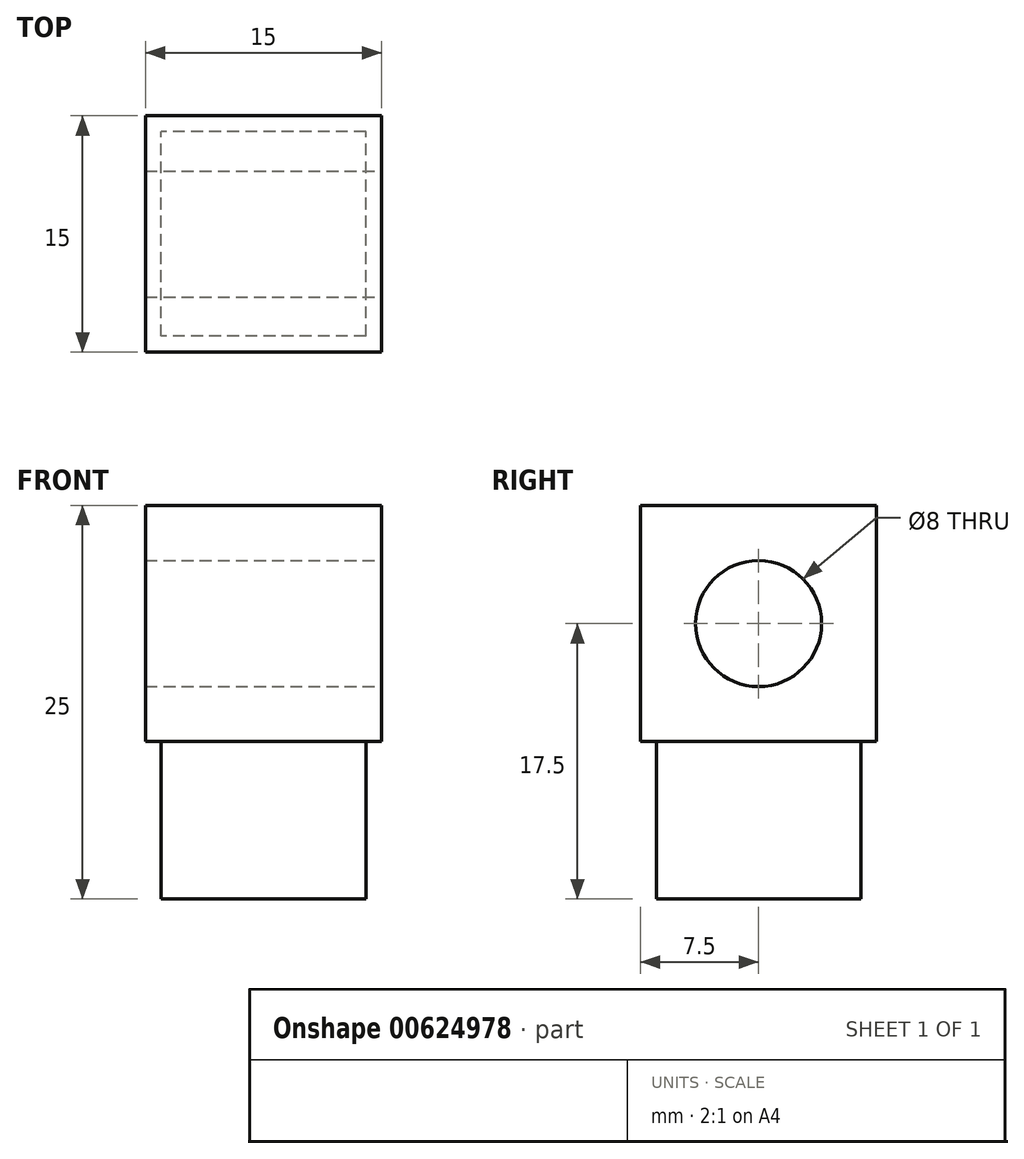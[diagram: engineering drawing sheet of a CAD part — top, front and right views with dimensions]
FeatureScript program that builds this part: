
annotation { "Feature Type Name" : "Feature", "Feature Type Description" : "" }
export const myFeature = defineFeature(function(context is Context, id is Id, definition is map)
    precondition{}
    {
        {
            var Q0;
            Q0=qCreatedBy(makeId("Top.planeOp"),FACE);
            var sketch = newSketch(context, id + "F0", { "sketchPlane" : qUnion([Q0])});
            skLineSegment(sketch, "E0.bottom", {"start": v(6.5, -6.5) * mm, "end": v(-6.5, -6.5) * mm});
            skLineSegment(sketch, "E0.top", {"start": v(6.5, 6.5) * mm, "end": v(-6.5, 6.5) * mm});
            skLineSegment(sketch, "E0.left", {"start": v(6.5, -6.5) * mm, "end": v(6.5, 6.5) * mm});
            skLineSegment(sketch, "E0.right", {"start": v(-6.5, -6.5) * mm, "end": v(-6.5, 6.5) * mm});
            skPoint(sketch, "E0.middle", {"position": v(0, 0) * mm});
            skSolve(sketch);
        }
        {
            var Q0;
            Q0=makeQuery(id+"F0.imprint","IMPRINT",FACE,{"disambiguationData":[TD([[makeQuery(id+"F0.imprint","IMPRINT",EDGE,{"derivedFrom":sQuery(id+"F0.wireOp",EDGE,"E0.bottom")}),-1.0]])]});
            extrude(context, id + "F1", {"entities" : qUnion([Q0]), "depth" : 10 * mm, "offsetDistance" : 25 * mm});
        }
        {
            var Q0;
            Q0=makeQuery(id+"F1.opExtrude","CAP_FACE",FACE,{"disambiguationData":[OSD([sQuery(id+"F0.wireOp",EDGE,"E0.bottom"),sQuery(id+"F0.wireOp",EDGE,"E0.top"),sQuery(id+"F0.wireOp",EDGE,"E0.left"),sQuery(id+"F0.wireOp",EDGE,"E0.right")])],"isStart":false});
            var sketch = newSketch(context, id + "F2", { "sketchPlane" : qUnion([Q0])});
            skLineSegment(sketch, "E1.bottom", {"start": v(7.5, -7.5) * mm, "end": v(-7.5, -7.5) * mm});
            skLineSegment(sketch, "E1.top", {"start": v(7.5, 7.5) * mm, "end": v(-7.5, 7.5) * mm});
            skLineSegment(sketch, "E1.left", {"start": v(7.5, -7.5) * mm, "end": v(7.5, 7.5) * mm});
            skLineSegment(sketch, "E1.right", {"start": v(-7.5, -7.5) * mm, "end": v(-7.5, 7.5) * mm});
            skPoint(sketch, "E1.middle", {"position": v(0, 0) * mm});
            skSolve(sketch);
        }
        {
            var Q0;
            Q0=makeQuery(id+"F2.imprint","IMPRINT",FACE,{"disambiguationData":[TD([[makeQuery(id+"F2.imprint","IMPRINT",EDGE,{"derivedFrom":makeQuery(id+"F1.opExtrude","CAP_EDGE",EDGE,{"disambiguationData":[OSD([sQuery(id+"F0.wireOp",EDGE,"E0.bottom")])],"isStart":false})}),-1.0]])]});
            var Q1;
            Q1=makeQuery(id+"F2.imprint","IMPRINT",FACE,{"disambiguationData":[TD([[makeQuery(id+"F2.imprint","IMPRINT",EDGE,{"derivedFrom":sQuery(id+"F2.wireOp",EDGE,"E1.bottom")}),-1.0]])]});
            extrude(context, id + "F3", {"entities" : qUnion([Q0, Q1]), "operationType" : NewBodyOperationType.ADD, "depth" : 15 * mm, "offsetDistance" : 25 * mm});
        }
        {
            var Q0;
            Q0=makeQuery(id+"F3.opExtrude","SWEPT_FACE",FACE,{"disambiguationData":[OSD([sQuery(id+"F2.wireOp",EDGE,"E1.left")])]});
            var sketch = newSketch(context, id + "F4", { "sketchPlane" : qUnion([Q0])});
            skLineSegment(sketch, "E2", {"start": v(-7.5, 25) * mm, "end": v(7.5, 10) * mm, "construction": true});
            skLineSegment(sketch, "E3", {"start": v(7.5, 25) * mm, "end": v(-7.5, 10) * mm, "construction": true});
            skPoint(sketch, "E4", {"position": v(0, 17.5) * mm});
            skCircle(sketch, "E5", {"center": v(0, 17.5) * mm, "radius": 4 * mm});
            skSolve(sketch);
        }
        {
            var Q0;
            Q0=makeQuery(id+"F4.imprint","IMPRINT",FACE,{"disambiguationData":[TD([[makeQuery(id+"F4.imprint","IMPRINT",EDGE,{"derivedFrom":sQuery(id+"F4.wireOp",EDGE,"E5")}),1.0]])]});
            extrude(context, id + "F5", {"entities" : qUnion([Q0]), "operationType" : NewBodyOperationType.REMOVE, "oppositeDirection" : true, "depth" : 25 * mm, "offsetDistance" : 25 * mm});
        }
    });
